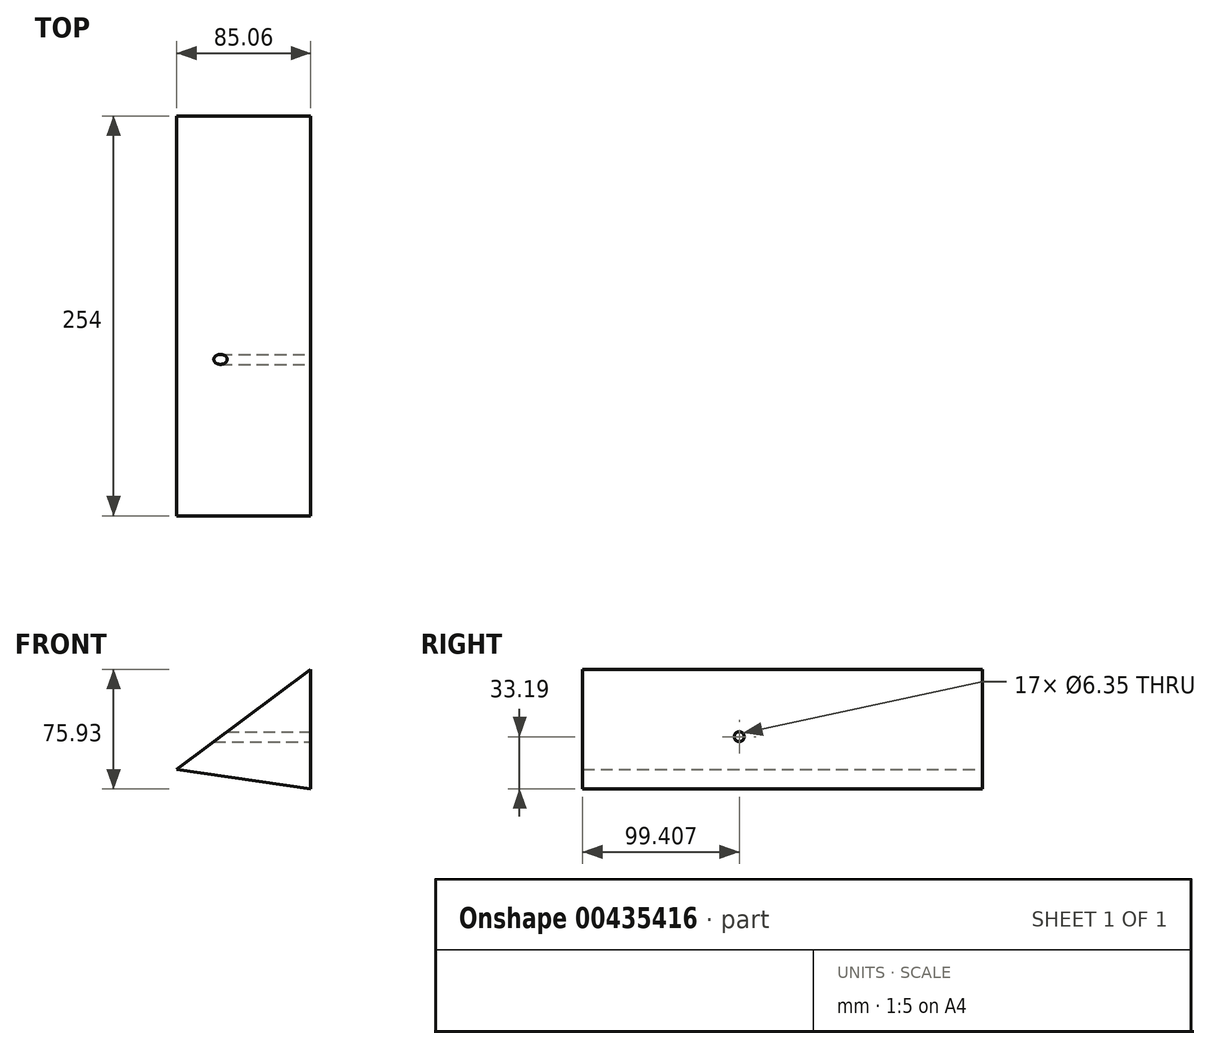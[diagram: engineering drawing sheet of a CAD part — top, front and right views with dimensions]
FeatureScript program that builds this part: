
annotation { "Feature Type Name" : "Feature", "Feature Type Description" : "" }
export const myFeature = defineFeature(function(context is Context, id is Id, definition is map)
    precondition{}
    {
        {
            var Q0;
            Q0=qCreatedBy(makeId("Front.planeOp"),FACE);
            var sketch = newSketch(context, id + "F0", { "sketchPlane" : qUnion([Q0])});
            skLineSegment(sketch, "E0", {"start": v(-48.34, -20.75) * mm, "end": v(36.72, 42.74) * mm});
            skLineSegment(sketch, "E1", {"start": v(36.72, 42.74) * mm, "end": v(36.72, -33.2) * mm});
            skLineSegment(sketch, "E2", {"start": v(36.72, -33.2) * mm, "end": v(-48.34, -20.75) * mm});
            skSolve(sketch);
        }
        {
            var Q0;
            Q0 = qSketchRegion(id + "F0", true);
            extrude(context, id + "F1", {"entities" : qUnion([Q0]), "depth" : 254 * mm});
        }
        {
            var Q0;
            Q0=makeQuery(id+"F1.opExtrude","SWEPT_FACE",FACE,{"disambiguationData":[OSD([sQuery(id+"F0.wireOp",EDGE,"E1")])]});
            var sketch = newSketch(context, id + "F2", { "sketchPlane" : qUnion([Q0])});
            skCircle(sketch, "E3", {"center": v(-154.6, 0) * mm, "radius": 22.94 * mm});
            skSolve(sketch);
        }
        {
            var Q0;
            Q0=sQuery(id+"F2.wireOp",VERTEX,"E3.center");
            var Q1;
            Q1=makeQuery(id+"F1.opExtrude","SWEPT_BODY",BODY,{"disambiguationData":[OSD([sQuery(id+"F0.wireOp",EDGE,"E0"),sQuery(id+"F0.wireOp",EDGE,"E1"),sQuery(id+"F0.wireOp",EDGE,"E2")])]});
            hole(context, id + "F3", {"style" : HoleStyle.SIMPLE, "endStyle" : HoleEndStyle.THROUGH, "holeDiameter" : 6.35 * mm, "isTappedThrough" : true, "tappedDepth" : 12.7 * mm, "tapClearance" : 3, "locations" : qUnion([Q0]), "scope" : qUnion([Q1])});
        }
    });
